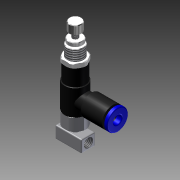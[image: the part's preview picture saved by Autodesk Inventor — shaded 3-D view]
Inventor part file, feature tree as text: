
AUTODESK INVENTOR PART (.ipt)
format: ipt  version: 2012 (Build 160160000, 160)  size: 583,680 bytes
history: native  units: in
note: dims shown in document units (in); Inventor stores cm internally (conversion verified against a paired STEP export)
features: plane x5, thread x5, split x4, fillet x3, other x2, sketch x2, move_body x1, extrude x1, hole x1, imported_body x1
ambient origin geometry x8: Origin, YZ Plane, XZ Plane, XY Plane, X Axis, Y Axis, Z Axis, Center Point
bodies: Solid1 (feature_tree), Solid2 (feature_tree), Solid3 (feature_tree), Solid4 (feature_tree), Solid5 (feature_tree), Solid6 (feature_tree), Solid7 (feature_tree), Solid8 (feature_tree), Solid9 (feature_tree)
feature tree (25):
  other  "ARJ1020F-M5-04-1.SAT1"
  plane  "Work Plane1"
  split  "Split1"
  thread  "Thread1"  [1 undecoded]
  thread  "Thread2"  [1 undecoded]
  thread  "Thread3"  [1 undecoded]
  thread  "Thread4"  [1 undecoded]
  plane  "Work Plane2"
  split  "Split2"
  move_body  "Move Body1"
  other  "Alias Freeform1"
  plane  "Work Plane3"
  plane  "Work Plane4"
  split  "Split3"
  split  "Split4"
  plane  "Work Plane5"
  extrude  "Extrusion1"  TaperAngle=0.0deg  [1 undecoded]
  fillet  "Fillet1"  [1 undecoded]
  fillet  "Fillet2"  [1 undecoded]
  fillet  "Fillet3"  Radius=0.0787in
  hole  "Hole2"  [1 undecoded]
  thread  "Thread6"  [1 undecoded]
  imported_body  "Base1"
  sketch  "Sketch1"  dims[d9=0.0in d10=0.0in d11=-0.0984in d12=0.0in d13=0.0in d14=0.0in d15=0.0787in]
  sketch  "Sketch5"  dims[d16=0.2559in d17=0.1378in d18=0.5118in d19=0.2362in d20=0.0in d24=0.0197in d25=0.0197in d36=0.0197in d42=0.1772in d43=0.1772in d44=0.2362in d45=0.1575in d46=0.0787in d47=90.0deg d48=0.3543in d49=0.8108in d50=0.3937in d51=0.0in]
note: 9 required parameter values undecoded (feature->parameter linkage not recoverable at this tier; creation-order binding heuristic only, values carry confidence <= 0.55)
